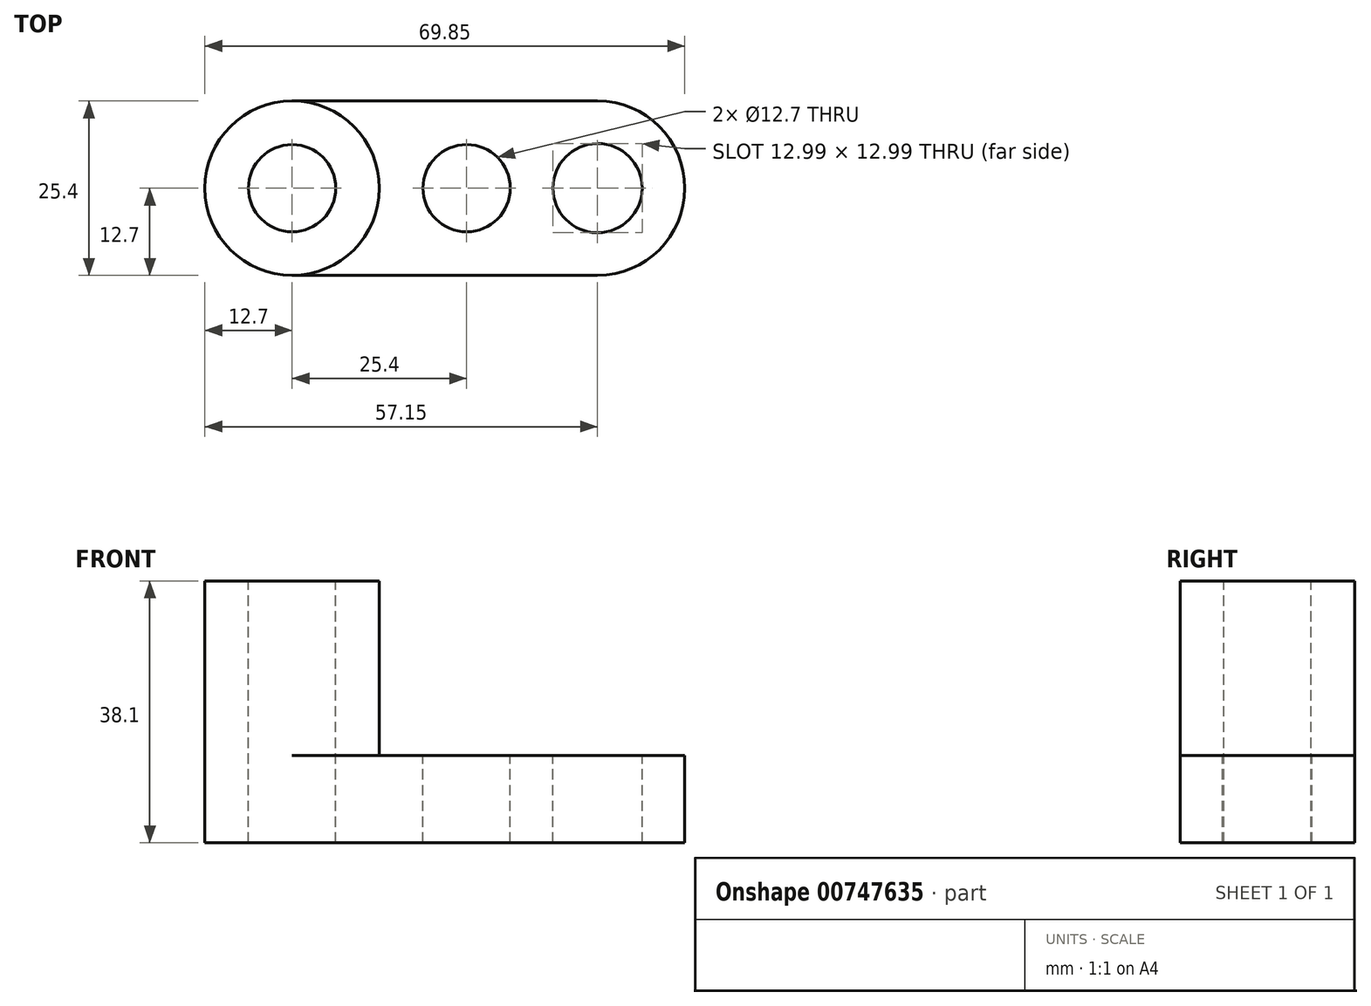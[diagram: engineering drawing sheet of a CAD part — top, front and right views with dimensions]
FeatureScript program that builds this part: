
annotation { "Feature Type Name" : "Feature", "Feature Type Description" : "" }
export const myFeature = defineFeature(function(context is Context, id is Id, definition is map)
    precondition{}
    {
        {
            var Q0;
            Q0=qCreatedBy(makeId("Front.planeOp"),FACE);
            var sketch = newSketch(context, id + "F0", { "sketchPlane" : qUnion([Q0])});
            skLineSegment(sketch, "E0", {"start": v(0, 0) * mm, "end": v(69.85, 0) * mm});
            skLineSegment(sketch, "E1", {"start": v(69.85, 0) * mm, "end": v(69.85, 38.1) * mm});
            skLineSegment(sketch, "E2", {"start": v(69.85, 38.1) * mm, "end": v(0, 38.1) * mm});
            skLineSegment(sketch, "E3", {"start": v(0, 38.1) * mm, "end": v(0, 0) * mm});
            skSolve(sketch);
        }
        {
            var Q0;
            Q0 = qSketchRegion(id + "F0", true);
            extrude(context, id + "F1", {"entities" : qUnion([Q0]), "oppositeDirection" : true, "depth" : 25.4 * mm, "offsetDistance" : 25.4 * mm});
        }
        {
            var Q0;
            Q0=makeQuery(id+"F1.opExtrude","CAP_FACE",FACE,{"disambiguationData":[OSD([sQuery(id+"F0.wireOp",EDGE,"E0"),sQuery(id+"F0.wireOp",EDGE,"E1"),sQuery(id+"F0.wireOp",EDGE,"E2"),sQuery(id+"F0.wireOp",EDGE,"E3")])],"isStart":true});
            var sketch = newSketch(context, id + "F2", { "sketchPlane" : qUnion([Q0])});
            skLineSegment(sketch, "E4", {"start": v(25.4, 38.1) * mm, "end": v(25.4, 12.7) * mm});
            skLineSegment(sketch, "E5", {"start": v(25.4, 12.7) * mm, "end": v(69.85, 12.7) * mm});
            skSolve(sketch);
        }
        {
            var Q0;
            Q0 = qSketchRegion(id + "F2", true);
            var Q1;
            {var subQ0=sQuery(id+"F2.wireOp",EDGE,"E4");Q1=makeQuery(id+"F2.imprint","IMPRINT",FACE,{"disambiguationData":[TD([[makeQuery(id+"F2.imprint","IMPRINT",EDGE,{"derivedFrom":subQ0}),1.0]])]});}
            extrude(context, id + "F3", {"entities" : qUnion([Q0, Q1]), "operationType" : NewBodyOperationType.REMOVE, "oppositeDirection" : true, "depth" : 25.4 * mm, "offsetDistance" : 25.4 * mm});
        }
        {
            var Q0;
            Q0=makeQuery(id+"F1.opExtrude","SWEPT_FACE",FACE,{"disambiguationData":[OSD([sQuery(id+"F0.wireOp",EDGE,"E2")])]});
            var sketch = newSketch(context, id + "F4", { "sketchPlane" : qUnion([Q0])});
            skCircle(sketch, "E6", {"center": v(12.7, 12.7) * mm, "radius": 12.7 * mm});
            skPoint(sketch, "E6.centerSnap0", {"position": v(0, 12.7) * mm});
            skPoint(sketch, "E6.centerSnap1", {"position": v(12.7, 25.4) * mm});
            skSolve(sketch);
        }
        {
            var Q0;
            {var subQ0=sQuery(id+"F4.wireOp",EDGE,"E6");var subQ1=sQuery(id+"F0.wireOp",EDGE,"E2");var subQ2=makeQuery(id+"F1.opExtrude","CAP_EDGE",EDGE,{"disambiguationData":[OSD([subQ1])],"isStart":false});var subQ3=makeQuery(id+"F4.imprint","INTERSECT",VERTEX,{"derivedFrom":[subQ2,subQ0]});Q0=makeQuery(id+"F4.imprint","IMPRINT",FACE,{"disambiguationData":[TD([[makeQuery(id+"F4.imprint","IMPRINT",EDGE,{"disambiguationData":[TD([[subQ3,-1.0]])],"derivedFrom":subQ0}),-1.0]])]});}
            var Q1;
            {var subQ0=sQuery(id+"F4.wireOp",EDGE,"E6");var subQ1=sQuery(id+"F0.wireOp",EDGE,"E2");var subQ4=makeQuery(id+"F1.opExtrude","CAP_EDGE",EDGE,{"disambiguationData":[OSD([subQ1])],"isStart":true});var subQ5=makeQuery(id+"F4.imprint","INTERSECT",VERTEX,{"derivedFrom":[subQ4,subQ0]});Q1=makeQuery(id+"F4.imprint","IMPRINT",FACE,{"disambiguationData":[TD([[makeQuery(id+"F4.imprint","IMPRINT",EDGE,{"disambiguationData":[TD([[subQ5,1.0]])],"derivedFrom":subQ0}),-1.0]])]});}
            var Q2;
            {var subQ0=sQuery(id+"F4.wireOp",EDGE,"E6");var subQ1=sQuery(id+"F0.wireOp",EDGE,"E2");var subQ4=makeQuery(id+"F1.opExtrude","CAP_EDGE",EDGE,{"disambiguationData":[OSD([subQ1])],"isStart":true});var subQ5=makeQuery(id+"F4.imprint","INTERSECT",VERTEX,{"derivedFrom":[subQ4,subQ0]});Q2=makeQuery(id+"F4.imprint","IMPRINT",FACE,{"disambiguationData":[TD([[makeQuery(id+"F4.imprint","IMPRINT",EDGE,{"disambiguationData":[TD([[subQ5,-1.0]])],"derivedFrom":subQ0}),-1.0]])]});}
            var Q3;
            {var subQ0=sQuery(id+"F4.wireOp",EDGE,"E6");var subQ1=sQuery(id+"F0.wireOp",EDGE,"E2");var subQ2=makeQuery(id+"F1.opExtrude","CAP_EDGE",EDGE,{"disambiguationData":[OSD([subQ1])],"isStart":false});var subQ3=makeQuery(id+"F4.imprint","INTERSECT",VERTEX,{"derivedFrom":[subQ2,subQ0]});Q3=makeQuery(id+"F4.imprint","IMPRINT",FACE,{"disambiguationData":[TD([[makeQuery(id+"F4.imprint","IMPRINT",EDGE,{"disambiguationData":[TD([[subQ3,1.0]])],"derivedFrom":subQ0}),-1.0]])]});}
            extrude(context, id + "F5", {"entities" : qUnion([Q0, Q1, Q2, Q3]), "operationType" : NewBodyOperationType.REMOVE, "oppositeDirection" : true, "depth" : 25.4 * mm, "offsetDistance" : 25.4 * mm});
        }
        {
            var Q0;
            {var subQ0=sQuery(id+"F0.wireOp",EDGE,"E2");var subQ1=makeQuery(id+"F1.opExtrude","CAP_EDGE",EDGE,{"disambiguationData":[OSD([subQ0])],"isStart":false});var subQ2=sQuery(id+"F0.wireOp",EDGE,"E3");var subQ3=makeQuery(id+"F1.opExtrude","SWEPT_EDGE",EDGE,{"disambiguationData":[OSD([subQ0,subQ2])]});var subQ4=makeQuery(id+"F4.imprint","INTERSECT",VERTEX,{"derivedFrom":[subQ3,subQ1]});var subQ5=sQuery(id+"F4.wireOp",EDGE,"E6");var subQ6=makeQuery(id+"F4.imprint","INTERSECT",VERTEX,{"derivedFrom":[subQ1,subQ5]});Q0=makeQuery(id+"F5.boolean.opBoolean","COPY",FACE,{"derivedFrom":makeQuery(id+"F5.opExtrude","CAP_FACE",FACE,{"disambiguationData":[OSD([subQ0,subQ2,subQ5]),TDD([makeQuery(id+"F4.imprint","IMPRINT",EDGE,{"disambiguationData":[TD([[subQ6,-1.0]])],"derivedFrom":subQ5}),makeQuery(id+"F4.imprint","IMPRINT",EDGE,{"disambiguationData":[TD([[subQ4,-1.0]])],"derivedFrom":subQ3}),makeQuery(id+"F4.imprint","IMPRINT",EDGE,{"disambiguationData":[TD([[subQ6,-1.0]])],"derivedFrom":subQ1})])],"isStart":false})});}
            var Q1;
            {var subQ0=sQuery(id+"F0.wireOp",EDGE,"E2");var subQ1=makeQuery(id+"F1.opExtrude","CAP_EDGE",EDGE,{"disambiguationData":[OSD([subQ0])],"isStart":true});var subQ2=sQuery(id+"F0.wireOp",EDGE,"E3");var subQ3=makeQuery(id+"F1.opExtrude","SWEPT_EDGE",EDGE,{"disambiguationData":[OSD([subQ0,subQ2])]});var subQ4=makeQuery(id+"F4.imprint","INTERSECT",VERTEX,{"derivedFrom":[subQ3,subQ1]});var subQ5=sQuery(id+"F4.wireOp",EDGE,"E6");var subQ6=makeQuery(id+"F4.imprint","INTERSECT",VERTEX,{"derivedFrom":[subQ1,subQ5]});Q1=makeQuery(id+"F5.boolean.opBoolean","COPY",FACE,{"derivedFrom":makeQuery(id+"F5.opExtrude","CAP_FACE",FACE,{"disambiguationData":[OSD([subQ0,subQ2,subQ5]),TDD([makeQuery(id+"F4.imprint","IMPRINT",EDGE,{"disambiguationData":[TD([[subQ6,1.0]])],"derivedFrom":subQ5}),makeQuery(id+"F4.imprint","IMPRINT",EDGE,{"disambiguationData":[TD([[subQ4,1.0]])],"derivedFrom":subQ3}),makeQuery(id+"F4.imprint","IMPRINT",EDGE,{"disambiguationData":[TD([[subQ6,-1.0]])],"derivedFrom":subQ1})])],"isStart":false})});}
            extrude(context, id + "F6", {"entities" : qUnion([Q0, Q1]), "operationType" : NewBodyOperationType.REMOVE, "oppositeDirection" : true, "depth" : 25.4 * mm, "offsetDistance" : 25.4 * mm});
        }
        {
            var Q0;
            {var subQ0=sQuery(id+"F0.wireOp",EDGE,"E2");var subQ1=makeQuery(id+"F1.opExtrude","CAP_EDGE",EDGE,{"disambiguationData":[OSD([subQ0])],"isStart":true});var subQ2=sQuery(id+"F2.wireOp",EDGE,"E4");var subQ3=makeQuery(id+"F3.boolean.opBoolean","COPY",EDGE,{"derivedFrom":makeQuery(id+"F3.opExtrude","SWEPT_EDGE",EDGE,{"disambiguationData":[OSD([subQ0,subQ2])]})});var subQ4=makeQuery(id+"F4.imprint","INTERSECT",VERTEX,{"derivedFrom":[subQ3,subQ1]});var subQ5=sQuery(id+"F4.wireOp",EDGE,"E6");var subQ6=makeQuery(id+"F4.imprint","INTERSECT",VERTEX,{"derivedFrom":[subQ1,subQ5]});var subQ8=makeQuery(id+"F1.opExtrude","CAP_EDGE",EDGE,{"disambiguationData":[OSD([subQ0])],"isStart":false});var subQ9=makeQuery(id+"F4.imprint","INTERSECT",VERTEX,{"derivedFrom":[subQ3,subQ8]});var subQ10=makeQuery(id+"F4.imprint","INTERSECT",VERTEX,{"derivedFrom":[subQ8,subQ5]});Q0=makeQuery(id+"F5.boolean.opBoolean","MERGE",FACE,{"derivedFrom":[makeQuery(id+"F3.boolean.opBoolean","COPY",FACE,{"derivedFrom":makeQuery(id+"F3.opExtrude","SWEPT_FACE",FACE,{"disambiguationData":[OSD([sQuery(id+"F2.wireOp",EDGE,"E5")])]})})],"fromTools":[makeQuery(id+"F5.opExtrude","CAP_FACE",FACE,{"disambiguationData":[OSD([subQ0,subQ2,subQ5]),TDD([makeQuery(id+"F4.imprint","IMPRINT",EDGE,{"disambiguationData":[TD([[subQ10,1.0]])],"derivedFrom":subQ5}),makeQuery(id+"F4.imprint","IMPRINT",EDGE,{"disambiguationData":[TD([[subQ9,-1.0]])],"derivedFrom":subQ3}),makeQuery(id+"F4.imprint","IMPRINT",EDGE,{"disambiguationData":[TD([[subQ10,1.0]])],"derivedFrom":subQ8})])],"isStart":false}),makeQuery(id+"F5.opExtrude","CAP_FACE",FACE,{"disambiguationData":[OSD([subQ0,subQ2,subQ5]),TDD([makeQuery(id+"F4.imprint","IMPRINT",EDGE,{"disambiguationData":[TD([[subQ6,-1.0]])],"derivedFrom":subQ5}),makeQuery(id+"F4.imprint","IMPRINT",EDGE,{"disambiguationData":[TD([[subQ4,1.0]])],"derivedFrom":subQ3}),makeQuery(id+"F4.imprint","IMPRINT",EDGE,{"disambiguationData":[TD([[subQ6,1.0]])],"derivedFrom":subQ1})])],"isStart":false})]});}
            var sketch = newSketch(context, id + "F7", { "sketchPlane" : qUnion([Q0])});
            skArc(sketch, "E7", {"start": v(57.15, 0) * mm, "mid": v(69.85, 12.7) * mm, "end": v(57.15, 25.4) * mm});
            skCircle(sketch, "E8", {"center": v(38.1, 12.7) * mm, "radius": 6.35 * mm});
            skPoint(sketch, "E8.centerSnap0", {"position": v(25.4, 12.7) * mm});
            skCircle(sketch, "E9", {"center": v(57.15, 12.7) * mm, "radius": 6.5 * mm});
            skLineSegment(sketch, "E10", {"start": v(57.15, 19.2) * mm, "end": v(38.1, 19.05) * mm});
            skLineSegment(sketch, "E11", {"start": v(57.15, 6.2) * mm, "end": v(38.1, 6.35) * mm});
            skSolve(sketch);
        }
        {
            var Q0;
            {var subQ0=sQuery(id+"F7.wireOp",EDGE,"E7");var subQ3=sQuery(id+"F2.wireOp",EDGE,"E5");var subQ6=makeQuery(id+"F3.boolean.opBoolean","COPY",EDGE,{"derivedFrom":makeQuery(id+"F3.opExtrude","SWEPT_EDGE",EDGE,{"disambiguationData":[OSD([sQuery(id+"F0.wireOp",EDGE,"E1"),subQ3])]})});var subQ7=makeQuery(id+"F7.imprint","INTERSECT",VERTEX,{"derivedFrom":[subQ6,subQ0]});Q0=makeQuery(id+"F7.imprint","IMPRINT",FACE,{"disambiguationData":[TD([[makeQuery(id+"F7.imprint","IMPRINT",EDGE,{"disambiguationData":[TD([[subQ7,-1.0]])],"derivedFrom":subQ0}),-1.0]])]});}
            var Q1;
            {var subQ0=sQuery(id+"F7.wireOp",EDGE,"E7");var subQ3=sQuery(id+"F2.wireOp",EDGE,"E5");var subQ6=makeQuery(id+"F3.boolean.opBoolean","COPY",EDGE,{"derivedFrom":makeQuery(id+"F3.opExtrude","SWEPT_EDGE",EDGE,{"disambiguationData":[OSD([sQuery(id+"F0.wireOp",EDGE,"E1"),subQ3])]})});var subQ7=makeQuery(id+"F7.imprint","INTERSECT",VERTEX,{"derivedFrom":[subQ6,subQ0]});Q1=makeQuery(id+"F7.imprint","IMPRINT",FACE,{"disambiguationData":[TD([[makeQuery(id+"F7.imprint","IMPRINT",EDGE,{"disambiguationData":[TD([[subQ7,1.0]])],"derivedFrom":subQ0}),-1.0]])]});}
            var Q2;
            {var subQ0=sQuery(id+"F7.wireOp",EDGE,"E8");var subQ1=makeQuery(id+"F7.imprint","INTERSECT",VERTEX,{"derivedFrom":[subQ0,sQuery(id+"F7.wireOp",EDGE,"E10")]});Q2=makeQuery(id+"F7.imprint","IMPRINT",FACE,{"disambiguationData":[TD([[makeQuery(id+"F7.imprint","IMPRINT",EDGE,{"disambiguationData":[TD([[subQ1,-1.0]])],"derivedFrom":subQ0}),1.0]])]});}
            var Q3;
            {var subQ0=sQuery(id+"F7.wireOp",EDGE,"E10");Q3=makeQuery(id+"F7.imprint","IMPRINT",FACE,{"disambiguationData":[TD([[makeQuery(id+"F7.imprint","IMPRINT",EDGE,{"derivedFrom":subQ0}),1.0]])]});}
            var Q4;
            {var subQ0=sQuery(id+"F7.wireOp",EDGE,"E9");var subQ2=makeQuery(id+"F7.imprint","IMPRINT",VERTEX,{"disambiguationData":[OD(0.0)],"derivedFrom":subQ0});Q4=makeQuery(id+"F7.imprint","IMPRINT",FACE,{"disambiguationData":[TD([[makeQuery(id+"F7.imprint","IMPRINT",EDGE,{"disambiguationData":[TD([[subQ2,1.0]])],"derivedFrom":subQ0}),1.0]])]});}
            extrude(context, id + "F8", {"entities" : qUnion([Q0, Q1, Q2, Q3, Q4]), "operationType" : NewBodyOperationType.REMOVE, "oppositeDirection" : true, "depth" : 25.4 * mm, "offsetDistance" : 25.4 * mm});
        }
        {
            var Q0;
            Q0=makeQuery(id+"F1.opExtrude","SWEPT_FACE",FACE,{"disambiguationData":[OSD([sQuery(id+"F0.wireOp",EDGE,"E2")])]});
            var sketch = newSketch(context, id + "F9", { "sketchPlane" : qUnion([Q0])});
            skCircle(sketch, "E12", {"center": v(12.7, 12.7) * mm, "radius": 6.35 * mm});
            skSolve(sketch);
        }
        {
            var Q0;
            Q0=makeQuery(id+"F9.imprint","IMPRINT",FACE,{"disambiguationData":[TD([[makeQuery(id+"F9.imprint","IMPRINT",EDGE,{"derivedFrom":sQuery(id+"F9.wireOp",EDGE,"E12")}),1.0]])]});
            extrude(context, id + "F10", {"entities" : qUnion([Q0]), "operationType" : NewBodyOperationType.REMOVE, "oppositeDirection" : true, "depth" : 50.8 * mm, "offsetDistance" : 25.4 * mm});
        }
    });
